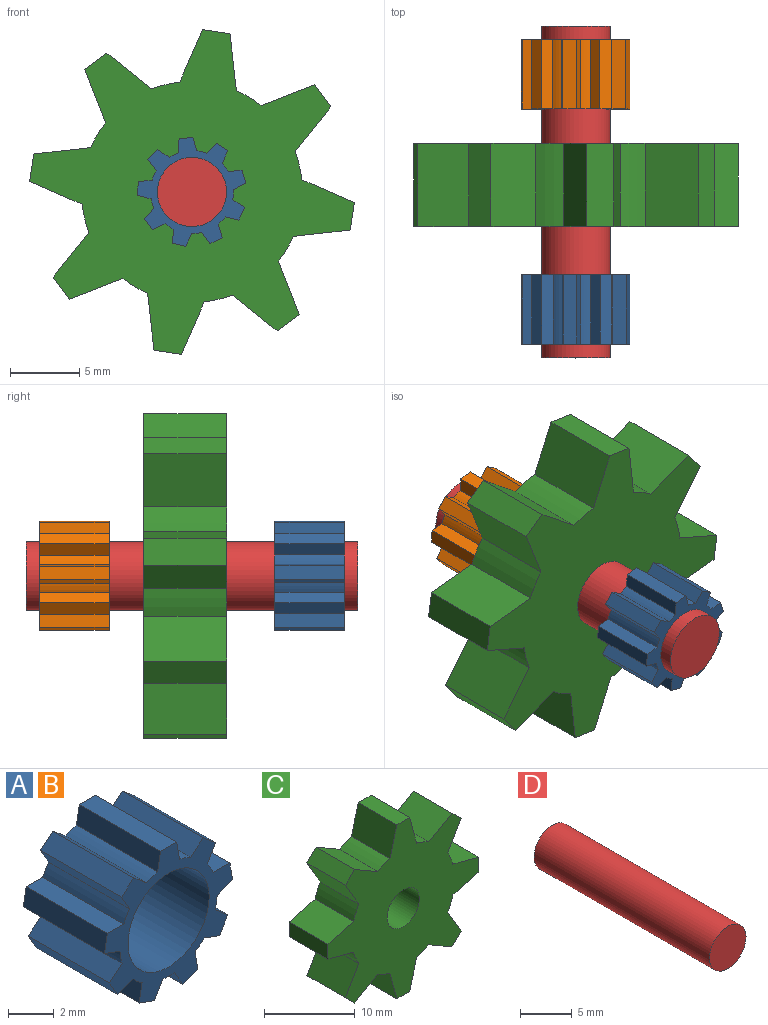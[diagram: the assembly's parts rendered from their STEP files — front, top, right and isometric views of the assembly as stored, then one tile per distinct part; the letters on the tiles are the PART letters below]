
ASSEMBLY  parts=4 mates=3
PART A: 39 faces, bbox 7.9x5x7.8 mm
  f0: cylinder r=3mm len=5mm, axis (0,1,0), area 3.7mm2, adj f1,f35,f37,f38
  f1: plane 5x1mm, normal (0.98,0,0.17), area 5.1mm2, adj f0,f2,f37,f38
  f2: plane 5x1mm, normal (0,0,1), area 5mm2, adj f1,f3,f37,f38
  f3: plane 5x1mm, normal (-0.98,0,0.17), area 5.1mm2, adj f2,f4,f37,f38
  f4: cylinder r=3mm len=5mm, axis (0,1,0), area 3.7mm2, adj f3,f5,f37,f38
  f5: plane 5x0.78mm, normal (0.64,0,0.77), area 5.1mm2, adj f4,f6,f37,f38
  f6: plane 5x0.77mm, normal (-0.64,0,0.77), area 5mm2, adj f5,f7,f37,f38
  f7: plane 5x0.88mm, normal (-0.87,0,-0.5), area 5.1mm2, adj f6,f8,f37,f38
  f8: cylinder r=3mm len=5mm, axis (0,1,0), area 3.7mm2, adj f7,f9,f37,f38
  f9: plane 5x1.02mm, normal (0,0,1), area 5.1mm2, adj f8,f10,f37,f38
  f10: plane 5x0.99mm, normal (-0.98,0,0.17), area 5mm2, adj f9,f11,f37,f38
  f11: plane 5x0.95mm, normal (-0.34,0,-0.94), area 5.1mm2, adj f10,f12,f37,f38
  f12: cylinder r=3mm len=5mm, axis (0,1,0), area 3.7mm2, adj f11,f13,f37,f38
  f13: plane 5x0.78mm, normal (-0.64,0,0.77), area 5.1mm2, adj f12,f14,f37,f38
  f14: plane 5x0.87mm, normal (-0.87,0,-0.5), area 5mm2, adj f13,f15,f37,f38
  f15: plane 5x0.95mm, normal (0.34,0,-0.94), area 5.1mm2, adj f14,f16,f37,f38
  f16: cylinder r=3mm len=5mm, axis (0,1,0), area 3.7mm2, adj f15,f17,f37,f38
  f17: plane 5x1mm, normal (-0.98,0,0.17), area 5.1mm2, adj f16,f18,f37,f38
  f18: plane 5x0.94mm, normal (-0.34,0,-0.94), area 5mm2, adj f17,f19,f37,f38
  f19: plane 5x0.88mm, normal (0.87,0,-0.5), area 5.1mm2, adj f18,f20,f37,f38
  f20: cylinder r=3mm len=5mm, axis (0,1,0), area 3.7mm2, adj f19,f21,f37,f38
  f21: plane 5x0.88mm, normal (-0.87,0,-0.5), area 5.1mm2, adj f20,f22,f37,f38
  f22: plane 5x0.94mm, normal (0.34,0,-0.94), area 5mm2, adj f21,f23,f37,f38
  f23: plane 5x1mm, normal (0.98,0,0.17), area 5.1mm2, adj f22,f24,f37,f38
  f24: cylinder r=3mm len=5mm, axis (0,1,0), area 3.7mm2, adj f23,f25,f37,f38
  f25: plane 5x0.95mm, normal (-0.34,0,-0.94), area 5.1mm2, adj f24,f26,f37,f38
  f26: plane 5x0.87mm, normal (0.87,0,-0.5), area 5mm2, adj f25,f27,f37,f38
  f27: plane 5x0.78mm, normal (0.64,0,0.77), area 5.1mm2, adj f26,f28,f37,f38
  f28: cylinder r=3mm len=5mm, axis (0,1,0), area 3.7mm2, adj f27,f29,f37,f38
  f29: plane 5x0.95mm, normal (0.34,0,-0.94), area 5.1mm2, adj f28,f30,f37,f38
  f30: plane 5x0.99mm, normal (0.98,0,0.17), area 5mm2, adj f29,f31,f37,f38
  f31: plane 5x1.02mm, normal (0,0,1), area 5.1mm2, adj f30,f32,f37,f38
  f32: cylinder r=3mm len=5mm, axis (0,1,0), area 3.7mm2, adj f31,f33,f37,f38
  f33: plane 5x0.88mm, normal (0.87,0,-0.5), area 5.1mm2, adj f32,f34,f37,f38
  f34: plane 5x0.77mm, normal (0.64,0,0.77), area 5mm2, adj f33,f35,f37,f38
  f35: plane 5x0.78mm, normal (-0.64,0,0.77), area 5.1mm2, adj f0,f34,f37,f38
  f36: cylinder r=2.5mm len=5mm, axis (0,1,0), area 78.5mm2, adj f37,f38
  f37: plane 7.9x7.78mm, normal (0,-1,0), area 18.6mm2, adj f0,f1,f2,f3,f4,f5,f6,f7
  f38: plane 7.9x7.78mm, normal (0,1,0), area 18.6mm2, adj f0,f1,f2,f3,f4,f5,f6,f7
PART B: same geometry as A
PART C: 35 faces, bbox 23.5x6x23.5 mm
  f0: plane 6x4mm, normal (-0.97,0,0.26), area 24.8mm2, adj f1,f31,f32,f33
  f1: cylinder r=8mm len=6mm, axis (0,-1,0), area 12.6mm2, adj f0,f2,f32,f33
  f2: plane 6x3.59mm, normal (0.5,0,0.87), area 24.8mm2, adj f1,f3,f32,f33
  f3: plane 6x1.41mm, normal (-0.71,0,0.71), area 12mm2, adj f2,f4,f32,f33
  f4: plane 6x3.59mm, normal (-0.87,0,-0.5), area 24.8mm2, adj f3,f5,f32,f33
  f5: cylinder r=8mm len=6mm, axis (0,-1,0), area 12.6mm2, adj f4,f6,f32,f33
  f6: plane 6x4mm, normal (-0.26,0,0.97), area 24.8mm2, adj f5,f7,f32,f33
  f7: plane 6x2mm, normal (-1,0,0), area 12mm2, adj f6,f8,f32,f33
  f8: plane 6x4mm, normal (-0.26,0,-0.97), area 24.8mm2, adj f7,f9,f32,f33
  f9: cylinder r=8mm len=6mm, axis (0,-1,0), area 12.6mm2, adj f8,f10,f32,f33
  f10: plane 6x3.59mm, normal (-0.87,0,0.5), area 24.8mm2, adj f9,f11,f32,f33
  f11: plane 6x1.41mm, normal (-0.71,0,-0.71), area 12mm2, adj f10,f12,f32,f33
  f12: plane 6x3.59mm, normal (0.5,0,-0.87), area 24.8mm2, adj f11,f13,f32,f33
  f13: cylinder r=8mm len=6mm, axis (0,-1,0), area 12.6mm2, adj f12,f14,f32,f33
  f14: plane 6x4mm, normal (-0.97,0,-0.26), area 24.8mm2, adj f13,f15,f32,f33
  f15: plane 6x2mm, normal (0,0,-1), area 12mm2, adj f14,f16,f32,f33
  f16: plane 6x4mm, normal (0.97,0,-0.26), area 24.8mm2, adj f15,f17,f32,f33
  f17: cylinder r=8mm len=6mm, axis (0,-1,0), area 12.6mm2, adj f16,f18,f32,f33
  f18: plane 6x3.59mm, normal (-0.5,0,-0.87), area 24.8mm2, adj f17,f19,f32,f33
  f19: plane 6x1.41mm, normal (0.71,0,-0.71), area 12mm2, adj f18,f20,f32,f33
  f20: plane 6x3.59mm, normal (0.87,0,0.5), area 24.8mm2, adj f19,f21,f32,f33
  f21: cylinder r=8mm len=6mm, axis (0,-1,0), area 12.6mm2, adj f20,f22,f32,f33
  f22: plane 6x4mm, normal (0.26,0,-0.97), area 24.8mm2, adj f21,f23,f32,f33
  f23: plane 6x2mm, normal (1,0,0), area 12mm2, adj f22,f24,f32,f33
  f24: plane 6x4mm, normal (0.26,0,0.97), area 24.8mm2, adj f23,f25,f32,f33
  f25: cylinder r=8mm len=6mm, axis (0,-1,0), area 12.6mm2, adj f24,f26,f32,f33
  f26: plane 6x3.59mm, normal (0.87,0,-0.5), area 24.8mm2, adj f25,f27,f32,f33
  f27: plane 6x1.41mm, normal (0.71,0,0.71), area 12mm2, adj f26,f28,f32,f33
  f28: plane 6x3.59mm, normal (-0.5,0,0.87), area 24.8mm2, adj f27,f29,f32,f33
  f29: cylinder r=8mm len=6mm, axis (0,-1,0), area 12.6mm2, adj f28,f30,f32,f33
  f30: plane 6x4mm, normal (0.97,0,0.26), area 24.8mm2, adj f29,f31,f32,f33
  f31: plane 6x2mm, normal (0,0,1), area 12mm2, adj f0,f30,f32,f33
  f32: plane 23.45x23.45mm, normal (0,1,0), area 273.7mm2, adj f0,f1,f2,f3,f4,f5,f6,f7
  f33: plane 23.45x23.45mm, normal (0,-1,0), area 273.7mm2, adj f0,f1,f2,f3,f4,f5,f6,f7
  f34: cylinder r=2.5mm len=6mm, axis (0,-1,0), area 94.2mm2, adj f32,f33
PART D: 3 faces, bbox 5x24x5 mm
  f0: cylinder r=2.5mm len=24mm, axis (0,-1,0), area 377mm2, adj f1,f2
  f1: plane 5x5mm, normal (0,1,0), area 19.6mm2, adj f0
  f2: plane 5x5mm, normal (0,-1,0), area 19.6mm2, adj f0
PLACE A rot(axis=(0.89,0,-0.45),180deg) t=(-72.11,-22.09,47.28)mm
PLACE B rot(axis=(0.69,0,-0.73),180deg) t=(-73.41,-5.09,51.67)mm
PLACE C rot(axis=(0.89,0,-0.45),180deg) t=(-72.11,-6.59,47.28)mm
PLACE D rot(axis=(0.89,0,-0.45),180deg) t=(-72.11,-6.09,47.28)mm
MATE revolute A.f4 <-> D.f0  axis (0,-1,0) through (-66.66,-21.09,51.29)mm
MATE revolute B.f4 <-> D.f0  axis (0,1,0) through (-66.66,0.91,51.29)mm
MATE revolute C.f25 <-> D.f0  axis (0,-1,0) through (-66.66,-12.59,51.29)mm
